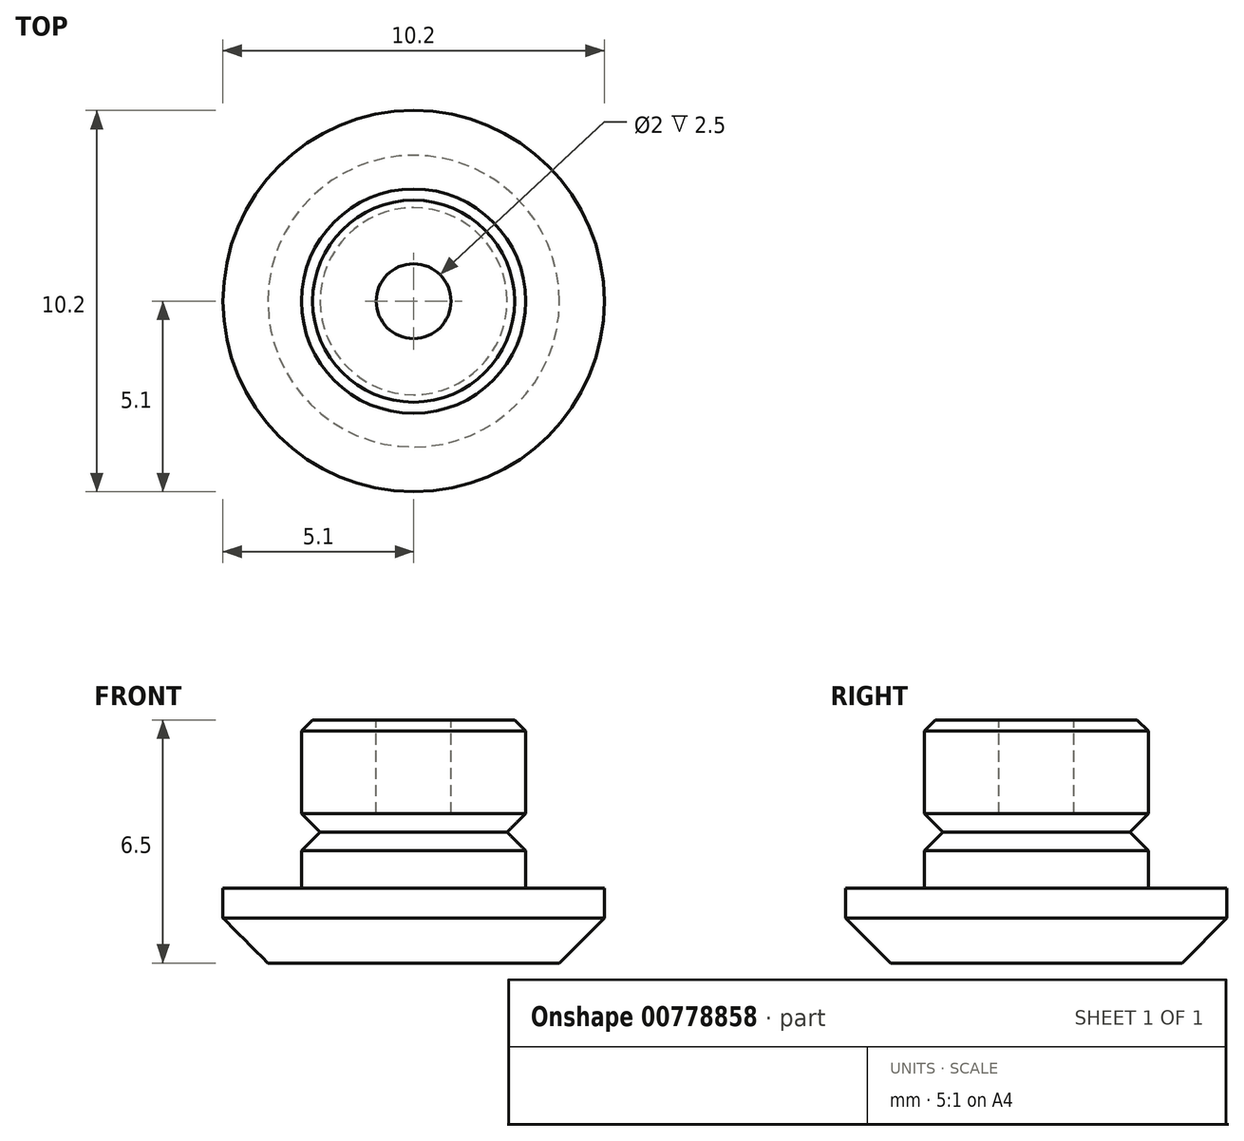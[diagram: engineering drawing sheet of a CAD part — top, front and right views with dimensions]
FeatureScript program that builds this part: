
annotation { "Feature Type Name" : "Feature", "Feature Type Description" : "" }
export const myFeature = defineFeature(function(context is Context, id is Id, definition is map)
    precondition{}
    {
        {
            var Q0;
            Q0=qCreatedBy(makeId("Front.planeOp"),FACE);
            var sketch = newSketch(context, id + "F0", { "sketchPlane" : qUnion([Q0])});
            skLineSegment(sketch, "E0", {"start": v(5.1, 0) * mm, "end": v(5.1, -2) * mm});
            skLineSegment(sketch, "E1", {"start": v(5.1, -2) * mm, "end": v(0, -2) * mm});
            skLineSegment(sketch, "E2", {"start": v(1, 2) * mm, "end": v(1, 4.5) * mm});
            skLineSegment(sketch, "E3", {"start": v(3, 1) * mm, "end": v(3, 0) * mm});
            skLineSegment(sketch, "E4.trimOffspring", {"start": v(3, 0) * mm, "end": v(5.1, 0) * mm});
            skLineSegment(sketch, "E5", {"start": v(0, 0) * mm, "end": v(0, -2) * mm});
            skLineSegment(sketch, "E6", {"start": v(1, 4.5) * mm, "end": v(3, 4.5) * mm});
            skLineSegment(sketch, "E7", {"start": v(3, 4.5) * mm, "end": v(3, 2) * mm});
            skLineSegment(sketch, "E8", {"start": v(3, 2) * mm, "end": v(2.5, 2) * mm});
            skLineSegment(sketch, "E9", {"start": v(2.5, 2) * mm, "end": v(2.5, 1) * mm});
            skLineSegment(sketch, "E10", {"start": v(2.5, 1) * mm, "end": v(3, 1) * mm});
            skLineSegment(sketch, "E11", {"start": v(0, 0) * mm, "end": v(0, 2) * mm});
            skLineSegment(sketch, "E12", {"start": v(0, 2) * mm, "end": v(1, 2) * mm});
            skSolve(sketch);
        }
        {
            var Q0;
            Q0=makeQuery(id+"F0.imprint","IMPRINT",FACE,{"disambiguationData":[TD([[makeQuery(id+"F0.imprint","IMPRINT",EDGE,{"derivedFrom":sQuery(id+"F0.wireOp",EDGE,"E0")}),-1.0]])]});
            var Q1;
            Q1=sQuery(id+"F0.wireOp",EDGE,"E5");
            revolve(context, id + "F1", {"surfaceOperationType" : NewSurfaceOperationType.NEW, "entities" : qUnion([Q0]), "axis" : qUnion([Q1]), "revolveType" : RevolveType.FULL});
        }
        {
            var Q0;
            Q0=makeQuery(id+"F1.opRevolve","SWEPT_EDGE",EDGE,{"disambiguationData":[OSD([sQuery(id+"F0.wireOp",EDGE,"E6"),sQuery(id+"F0.wireOp",EDGE,"E7")])]});
            chamfer(context, id + "F2", {"entities" : qUnion([Q0]), "width" : 0.3 * mm, "tangentPropagation" : true});
        }
        {
            var Q0;
            Q0=makeQuery(id+"F1.opRevolve","SWEPT_EDGE",EDGE,{"disambiguationData":[OSD([sQuery(id+"F0.wireOp",EDGE,"E8"),sQuery(id+"F0.wireOp",EDGE,"E9")])]});
            var Q1;
            Q1=makeQuery(id+"F1.opRevolve","SWEPT_EDGE",EDGE,{"disambiguationData":[OSD([sQuery(id+"F0.wireOp",EDGE,"E9"),sQuery(id+"F0.wireOp",EDGE,"E10")])]});
            chamfer(context, id + "F3", {"entities" : qUnion([Q0, Q1]), "width" : 0.5 * mm, "tangentPropagation" : true});
        }
        {
            var Q0;
            Q0=makeQuery(id+"F1.opRevolve","SWEPT_EDGE",EDGE,{"disambiguationData":[OSD([sQuery(id+"F0.wireOp",EDGE,"E0"),sQuery(id+"F0.wireOp",EDGE,"E1")])]});
            chamfer(context, id + "F4", {"entities" : qUnion([Q0]), "width" : 1.2 * mm, "tangentPropagation" : true});
        }
    });
